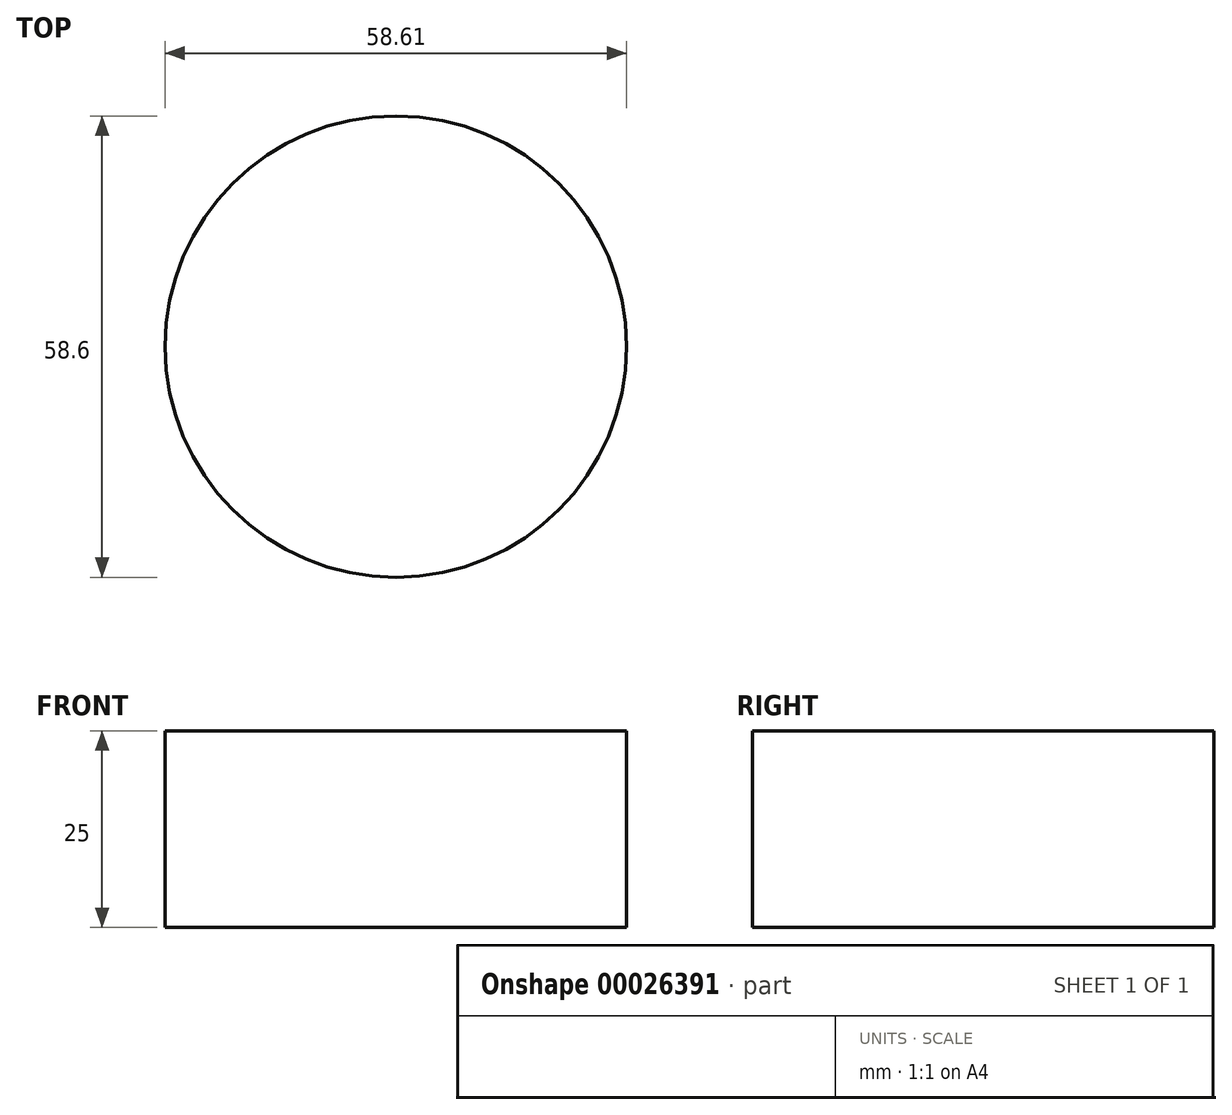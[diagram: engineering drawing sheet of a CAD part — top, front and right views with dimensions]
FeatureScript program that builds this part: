
annotation { "Feature Type Name" : "Feature", "Feature Type Description" : "" }
export const myFeature = defineFeature(function(context is Context, id is Id, definition is map)
    precondition{}
    {
        {
            var Q0;
            Q0=qCreatedBy(makeId("Top.planeOp"),FACE);
            var sketch = newSketch(context, id + "F0", { "sketchPlane" : qUnion([Q0])});
            skLineSegment(sketch, "E0.rect.bottom", {"start": v(-39.73, 29.3) * mm, "end": v(39.73, 29.3) * mm});
            skLineSegment(sketch, "E0.rect.top", {"start": v(-39.73, -29.3) * mm, "end": v(39.73, -29.3) * mm});
            skLineSegment(sketch, "E0.rect.left", {"start": v(-39.73, 29.3) * mm, "end": v(-39.73, -29.3) * mm});
            skLineSegment(sketch, "E0.rect.right", {"start": v(39.73, 29.3) * mm, "end": v(39.73, -29.3) * mm});
            skPoint(sketch, "E0.rect.middle", {"position": v(0, 0) * mm});
            skSolve(sketch);
        }
        {
            var Q0;
            Q0=makeQuery(id+"F0.imprint","IMPRINT",FACE,{"disambiguationData":[TD([[makeQuery(id+"F0.imprint","IMPRINT",EDGE,{"derivedFrom":sQuery(id+"F0.wireOp",EDGE,"E0.rect.bottom")}),-1.0]])]});
            var sketch = newSketch(context, id + "F1", { "sketchPlane" : qUnion([Q0])});
            skCircle(sketch, "E1", {"center": v(-10.42, 0) * mm, "radius": 29.3 * mm});
            skSolve(sketch);
        }
        {
            var Q0;
            Q0 = qSketchRegion(id + "F1", true);
            extrude(context, id + "F2", {"entities" : qUnion([Q0]), "depth" : 25 * mm});
        }
    });
